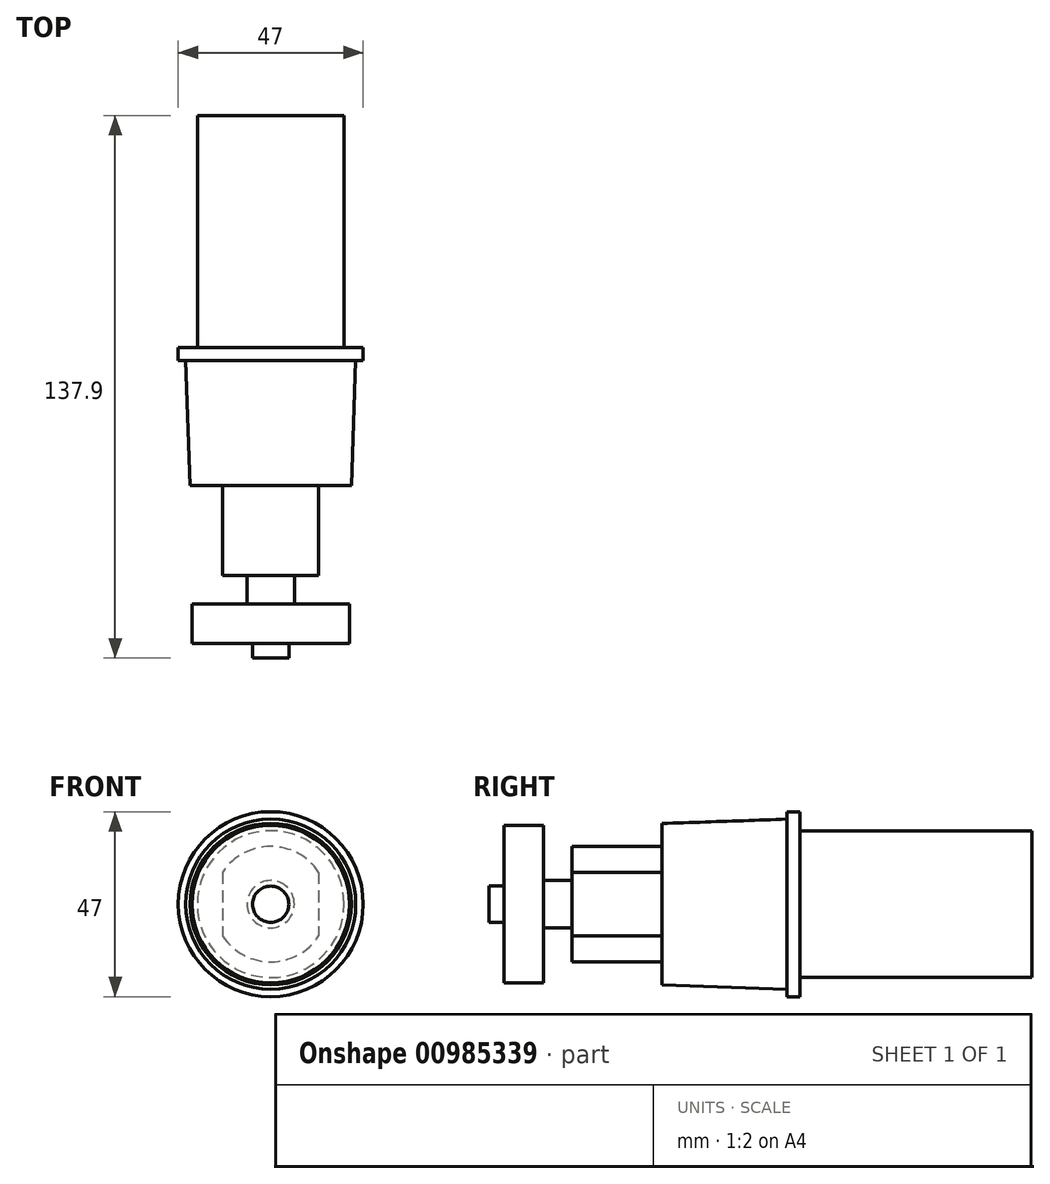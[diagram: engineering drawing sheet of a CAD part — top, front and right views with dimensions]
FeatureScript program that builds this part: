
annotation { "Feature Type Name" : "Feature", "Feature Type Description" : "" }
export const myFeature = defineFeature(function(context is Context, id is Id, definition is map)
    precondition{}
    {
        {
            var Q0;
            Q0=qCreatedBy(makeId("Front.planeOp"),FACE);
            var sketch = newSketch(context, id + "F0", { "sketchPlane" : qUnion([Q0])});
            skCircle(sketch, "E0", {"center": v(0, 0) * mm, "radius": 18.65 * mm});
            skSolve(sketch);
        }
        {
            var Q0;
            Q0=makeQuery(id+"F0.imprint","IMPRINT",FACE,{"disambiguationData":[TD([[makeQuery(id+"F0.imprint","IMPRINT",EDGE,{"derivedFrom":sQuery(id+"F0.wireOp",EDGE,"E0")}),1.0]])]});
            extrude(context, id + "F1", {"entities" : qUnion([Q0]), "oppositeDirection" : true, "depth" : 59 * mm});
        }
        {
            var Q0;
            Q0=qCreatedBy(makeId("Top.planeOp"),FACE);
            var sketch = newSketch(context, id + "F2", { "sketchPlane" : qUnion([Q0])});
            skLineSegment(sketch, "E1", {"start": v(0, 0) * mm, "end": v(0, -35) * mm});
            skLineSegment(sketch, "E2", {"start": v(0, -35) * mm, "end": v(20.5, -35) * mm});
            skLineSegment(sketch, "E3", {"start": v(20.5, -35) * mm, "end": v(21.6, -3.3) * mm});
            skLineSegment(sketch, "E4", {"start": v(21.6, -3.3) * mm, "end": v(23.5, -3.3) * mm});
            skLineSegment(sketch, "E5", {"start": v(23.5, -3.3) * mm, "end": v(23.5, 0) * mm});
            skLineSegment(sketch, "E6", {"start": v(23.5, 0) * mm, "end": v(0, 0) * mm});
            skSolve(sketch);
        }
        {
            var Q0;
            Q0=qSketchRegion(id+"F2",true);
            var Q1;
            Q1=sQuery(id+"F2.wireOp",EDGE,"E1");
            revolve(context, id + "F3", {"operationType" : NewBodyOperationType.ADD, "entities" : qUnion([Q0]), "axis" : qUnion([Q1]), "revolveType" : RevolveType.FULL});
        }
        {
            var Q0;
            Q0=makeQuery(id+"F3.opRevolve","SWEPT_FACE",FACE,{"disambiguationData":[OSD([sQuery(id+"F2.wireOp",EDGE,"E2")])]});
            var sketch = newSketch(context, id + "F4", { "sketchPlane" : qUnion([Q0])});
            skCircle(sketch, "E7", {"center": v(0, 0) * mm, "radius": 6 * mm});
            skLineSegment(sketch, "E8", {"start": v(-12.2, 8.11) * mm, "end": v(-12.2, -8.11) * mm});
            skLineSegment(sketch, "E9", {"start": v(12.2, 8.11) * mm, "end": v(12.2, -8.11) * mm});
            skCircle(sketch, "E10", {"center": v(0, 0) * mm, "radius": 14.65 * mm});
            skCircle(sketch, "E11", {"center": v(0, 0) * mm, "radius": 4.6 * mm});
            skSolve(sketch);
        }
        {
            var Q0;
            Q0=makeQuery(id+"F4.imprint","IMPRINT",FACE,{"disambiguationData":[TD([[makeQuery(id+"F4.imprint","IMPRINT",EDGE,{"derivedFrom":sQuery(id+"F4.wireOp",EDGE,"E7")}),-1.0]])]});
            var Q1;
            Q1=makeQuery(id+"F4.imprint","IMPRINT",FACE,{"disambiguationData":[TD([[makeQuery(id+"F4.imprint","IMPRINT",EDGE,{"derivedFrom":sQuery(id+"F4.wireOp",EDGE,"E7")}),1.0]])]});
            var Q2;
            Q2=makeQuery(id+"F4.imprint","IMPRINT",FACE,{"disambiguationData":[TD([[makeQuery(id+"F4.imprint","IMPRINT",EDGE,{"derivedFrom":sQuery(id+"F4.wireOp",EDGE,"E11")}),1.0]])]});
            extrude(context, id + "F5", {"entities" : qUnion([Q0, Q1, Q2]), "operationType" : NewBodyOperationType.ADD, "depth" : 22.9 * mm});
        }
        {
            var Q0;
            Q0=makeQuery(id+"F4.imprint","IMPRINT",FACE,{"disambiguationData":[TD([[makeQuery(id+"F4.imprint","IMPRINT",EDGE,{"derivedFrom":sQuery(id+"F4.wireOp",EDGE,"E7")}),1.0]])]});
            var Q1;
            Q1=makeQuery(id+"F4.imprint","IMPRINT",FACE,{"disambiguationData":[TD([[makeQuery(id+"F4.imprint","IMPRINT",EDGE,{"derivedFrom":sQuery(id+"F4.wireOp",EDGE,"E11")}),1.0]])]});
            extrude(context, id + "F6", {"entities" : qUnion([Q0, Q1]), "operationType" : NewBodyOperationType.ADD, "depth" : 30.1 * mm});
        }
        {
            var Q0;
            Q0=makeQuery(id+"F4.imprint","IMPRINT",FACE,{"disambiguationData":[TD([[makeQuery(id+"F4.imprint","IMPRINT",EDGE,{"derivedFrom":sQuery(id+"F4.wireOp",EDGE,"E11")}),1.0]])]});
            extrude(context, id + "F7", {"entities" : qUnion([Q0]), "operationType" : NewBodyOperationType.ADD, "depth" : 43.9 * mm});
        }
        {
            var Q0;
            Q0=makeQuery(id+"F6.opExtrude","CAP_FACE",FACE,{"disambiguationData":[OSD([sQuery(id+"F4.wireOp",EDGE,"E7")])],"isStart":false});
            var sketch = newSketch(context, id + "F8", { "sketchPlane" : qUnion([Q0])});
            skCircle(sketch, "E12", {"center": v(0, 0) * mm, "radius": 20 * mm});
            skSolve(sketch);
        }
        {
            var Q0;
            Q0=makeQuery(id+"F8.imprint","IMPRINT",FACE,{"disambiguationData":[TD([[makeQuery(id+"F8.imprint","IMPRINT",EDGE,{"derivedFrom":sQuery(id+"F8.wireOp",EDGE,"E12")}),1.0]])]});
            var Q1;
            {var subQ0=sQuery(id+"F4.wireOp",EDGE,"E7");Q1=makeQuery(id+"F8.imprint","IMPRINT",FACE,{"disambiguationData":[TD([[makeQuery(id+"F8.imprint","IMPRINT",EDGE,{"derivedFrom":makeQuery(id+"F6.opExtrude","CAP_EDGE",EDGE,{"disambiguationData":[OSD([subQ0])],"isStart":false})}),1.0]])]});}
            var Q2;
            Q2=makeQuery(id+"F7.opExtrude","CAP_FACE",FACE,{"disambiguationData":[OSD([sQuery(id+"F4.wireOp",EDGE,"E11")])],"isStart":false});
            extrude(context, id + "F9", {"entities" : qUnion([Q0, Q1]), "operationType" : NewBodyOperationType.ADD, "endBoundEntityFace" : qUnion([Q2]), "depth" : 10 * mm});
        }
    });
